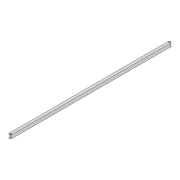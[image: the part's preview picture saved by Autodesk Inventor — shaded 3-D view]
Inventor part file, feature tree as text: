
AUTODESK INVENTOR PART (.ipt)
format: ipt  version: 2022 (Build 260153000, 153)  size: 84,992 bytes
history: native  units: mm
features: extrude x1, sketch x1
ambient origin geometry x8: Origin, YZ Plane, XZ Plane, XY Plane, X Axis, Y Axis, Z Axis, Center Point
bodies: Solid1 (feature_tree)
feature tree (2):
  extrude  "Extrusion1"  Depth=366.984mm
  sketch  "Sketch1"  dims[d0=6.0mm d1=366.984mm d2=3.0mm d3=3.0mm d4=8.0mm d5=0.0mm]
